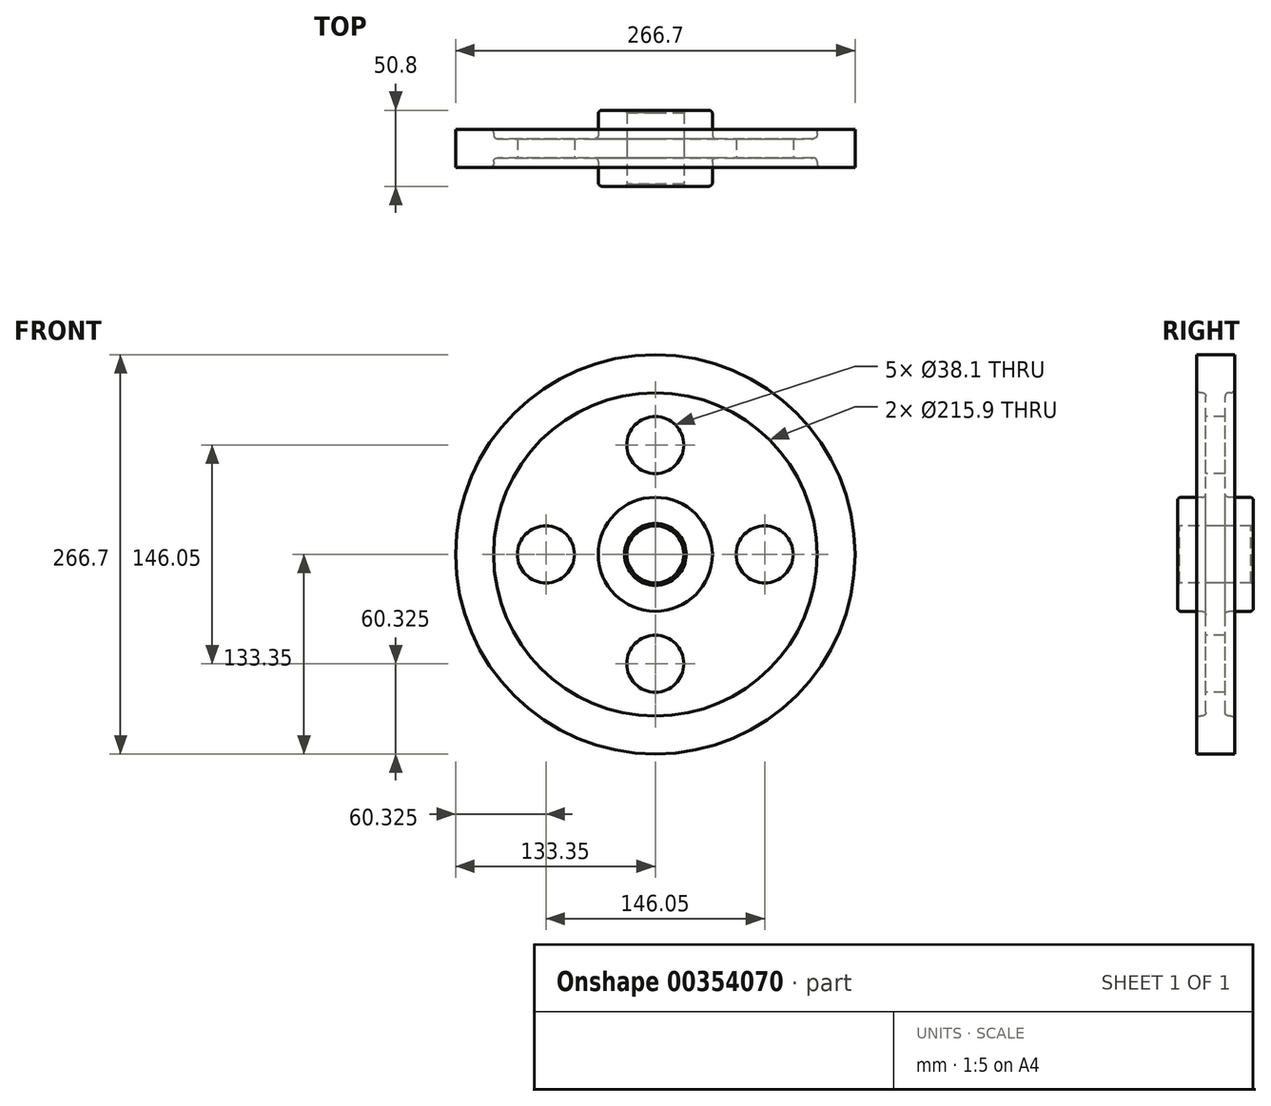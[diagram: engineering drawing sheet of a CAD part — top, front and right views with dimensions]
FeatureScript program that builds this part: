
annotation { "Feature Type Name" : "Feature", "Feature Type Description" : "" }
export const myFeature = defineFeature(function(context is Context, id is Id, definition is map)
    precondition{}
    {
        {
            var Q0;
            Q0=qCreatedBy(makeId("Right.planeOp"),FACE);
            var sketch = newSketch(context, id + "F0", { "sketchPlane" : qUnion([Q0])});
            skLineSegment(sketch, "E0", {"start": v(0, 0) * mm, "end": v(94.54, 0) * mm, "construction": true});
            skLineSegment(sketch, "E1.0", {"start": v(0, 19.05) * mm, "end": v(25.4, 19.05) * mm});
            skLineSegment(sketch, "E2.0", {"start": v(6.35, 38.1) * mm, "end": v(25.4, 38.1) * mm});
            skLineSegment(sketch, "E3.0", {"start": v(6.35, 107.95) * mm, "end": v(12.7, 107.95) * mm});
            skLineSegment(sketch, "E4.0", {"start": v(0, 133.35) * mm, "end": v(0, 133.35) * mm});
            skLineSegment(sketch, "E5", {"start": v(0, 0) * mm, "end": v(0, 133.35) * mm, "construction": true});
            skLineSegment(sketch, "E6.0", {"start": v(25.4, 19.05) * mm, "end": v(25.4, 38.1) * mm});
            skLineSegment(sketch, "E7.trimOffspring", {"start": v(12.7, 107.95) * mm, "end": v(12.7, 133.35) * mm});
            skLineSegment(sketch, "E8.trimOffspring", {"start": v(6.35, 38.1) * mm, "end": v(6.35, 107.95) * mm});
            skLineSegment(sketch, "E9.MirrorCS", {"start": v(-6.35, 38.1) * mm, "end": v(-6.35, 107.95) * mm});
            skLineSegment(sketch, "E10.MirrorCS", {"start": v(-12.7, 107.95) * mm, "end": v(-12.7, 133.35) * mm});
            skLineSegment(sketch, "E11.MirrorCS", {"start": v(-25.4, 19.05) * mm, "end": v(-25.4, 38.1) * mm});
            skLineSegment(sketch, "E12.MirrorCS", {"start": v(0, 19.05) * mm, "end": v(-25.4, 19.05) * mm});
            skLineSegment(sketch, "E13.MirrorCS", {"start": v(-6.35, 38.1) * mm, "end": v(-25.4, 38.1) * mm});
            skLineSegment(sketch, "E14", {"start": v(12.7, 133.35) * mm, "end": v(0, 133.35) * mm});
            skLineSegment(sketch, "E15", {"start": v(-12.7, 133.35) * mm, "end": v(0, 133.35) * mm});
            skLineSegment(sketch, "E16", {"start": v(-6.35, 107.95) * mm, "end": v(-12.7, 107.95) * mm});
            skSolve(sketch);
        }
        {
            var Q0;
            Q0=makeQuery(id+"F0.imprint","IMPRINT",FACE,{"disambiguationData":[TD([[makeQuery(id+"F0.imprint","IMPRINT",EDGE,{"derivedFrom":sQuery(id+"F0.wireOp",EDGE,"E1.0")}),1.0]])]});
            var Q1;
            Q1=sQuery(id+"F0.wireOp",EDGE,"E0");
            revolve(context, id + "F1", {"entities" : qUnion([Q0]), "axis" : qUnion([Q1]), "revolveType" : RevolveType.FULL});
        }
        {
            var Q0;
            Q0=makeQuery(id+"F1.opRevolve","SWEPT_FACE",FACE,{"disambiguationData":[OSD([sQuery(id+"F0.wireOp",EDGE,"E9.MirrorCS")])]});
            var sketch = newSketch(context, id + "F2", { "sketchPlane" : qUnion([Q0])});
            skLineSegment(sketch, "E17", {"start": v(0, 0) * mm, "end": v(0, 73.03) * mm});
            skCircle(sketch, "E18", {"center": v(0, 73.03) * mm, "radius": 19.05 * mm});
            skCircle(sketch, "E19.1.0", {"center": v(-73.03, 0) * mm, "radius": 19.05 * mm});
            skCircle(sketch, "E19.2.0", {"center": v(0, -73.03) * mm, "radius": 19.05 * mm});
            skCircle(sketch, "E19.3.0", {"center": v(73.03, 0) * mm, "radius": 19.05 * mm});
            skPoint(sketch, "E19.center", {"position": v(0, 0) * mm});
            skSolve(sketch);
        }
        {
            var Q0;
            Q0=makeQuery(id+"F2.imprint","IMPRINT",FACE,{"disambiguationData":[TD([[makeQuery(id+"F2.imprint","IMPRINT",EDGE,{"derivedFrom":sQuery(id+"F2.wireOp",EDGE,"E18")}),1.0]])]});
            var Q1;
            Q1=makeQuery(id+"F2.imprint","IMPRINT",FACE,{"disambiguationData":[TD([[makeQuery(id+"F2.imprint","IMPRINT",EDGE,{"derivedFrom":sQuery(id+"F2.wireOp",EDGE,"E19.1.0")}),1.0]])]});
            var Q2;
            Q2=makeQuery(id+"F2.imprint","IMPRINT",FACE,{"disambiguationData":[TD([[makeQuery(id+"F2.imprint","IMPRINT",EDGE,{"derivedFrom":sQuery(id+"F2.wireOp",EDGE,"E19.2.0")}),1.0]])]});
            var Q3;
            Q3=makeQuery(id+"F2.imprint","IMPRINT",FACE,{"disambiguationData":[TD([[makeQuery(id+"F2.imprint","IMPRINT",EDGE,{"derivedFrom":sQuery(id+"F2.wireOp",EDGE,"E19.3.0")}),1.0]])]});
            extrude(context, id + "F3", {"entities" : qUnion([Q0, Q1, Q2, Q3]), "operationType" : NewBodyOperationType.REMOVE, "oppositeDirection" : true, "depth" : 25.4 * mm});
        }
        {
            var Q0;
            Q0=makeQuery(id+"F1.opRevolve","SWEPT_EDGE",EDGE,{"disambiguationData":[OSD([sQuery(id+"F0.wireOp",EDGE,"E11.MirrorCS"),sQuery(id+"F0.wireOp",EDGE,"E13.MirrorCS")])]});
            var Q1;
            Q1=makeQuery(id+"F1.opRevolve","SWEPT_EDGE",EDGE,{"disambiguationData":[OSD([sQuery(id+"F0.wireOp",EDGE,"E9.MirrorCS"),sQuery(id+"F0.wireOp",EDGE,"E13.MirrorCS")])]});
            var Q2;
            Q2=makeQuery(id+"F1.opRevolve","SWEPT_EDGE",EDGE,{"disambiguationData":[OSD([sQuery(id+"F0.wireOp",EDGE,"E10.MirrorCS"),sQuery(id+"F0.wireOp",EDGE,"E16")])]});
            var Q3;
            Q3=makeQuery(id+"F1.opRevolve","SWEPT_EDGE",EDGE,{"disambiguationData":[OSD([sQuery(id+"F0.wireOp",EDGE,"E9.MirrorCS"),sQuery(id+"F0.wireOp",EDGE,"E16")])]});
            var Q4;
            Q4=makeQuery(id+"F1.opRevolve","SWEPT_EDGE",EDGE,{"disambiguationData":[OSD([sQuery(id+"F0.wireOp",EDGE,"E2.0"),sQuery(id+"F0.wireOp",EDGE,"E8.trimOffspring")])]});
            var Q5;
            Q5=makeQuery(id+"F1.opRevolve","SWEPT_EDGE",EDGE,{"disambiguationData":[OSD([sQuery(id+"F0.wireOp",EDGE,"E2.0"),sQuery(id+"F0.wireOp",EDGE,"E6.0")])]});
            var Q6;
            Q6=makeQuery(id+"F1.opRevolve","SWEPT_EDGE",EDGE,{"disambiguationData":[OSD([sQuery(id+"F0.wireOp",EDGE,"E3.0"),sQuery(id+"F0.wireOp",EDGE,"E8.trimOffspring")])]});
            var Q7;
            Q7=makeQuery(id+"F1.opRevolve","SWEPT_EDGE",EDGE,{"disambiguationData":[OSD([sQuery(id+"F0.wireOp",EDGE,"E3.0"),sQuery(id+"F0.wireOp",EDGE,"E7.trimOffspring")])]});
            fillet(context, id + "F4", {"entities" : qUnion([Q0, Q1, Q2, Q3, Q4, Q5, Q6, Q7]), "radius" : 2.54 * mm, "tangentPropagation" : true, "allowEdgeOverflow" : false});
        }
        {
            var Q0;
            Q0=makeQuery(id+"F1.opRevolve","SWEPT_EDGE",EDGE,{"disambiguationData":[OSD([sQuery(id+"F0.wireOp",EDGE,"E11.MirrorCS"),sQuery(id+"F0.wireOp",EDGE,"E12.MirrorCS")])]});
            var Q1;
            Q1=makeQuery(id+"F1.opRevolve","SWEPT_EDGE",EDGE,{"disambiguationData":[OSD([sQuery(id+"F0.wireOp",EDGE,"E1.0"),sQuery(id+"F0.wireOp",EDGE,"E6.0")])]});
            chamfer(context, id + "F5", {"entities" : qUnion([Q0, Q1]), "width" : 1.59 * mm, "tangentPropagation" : true});
        }
    });
